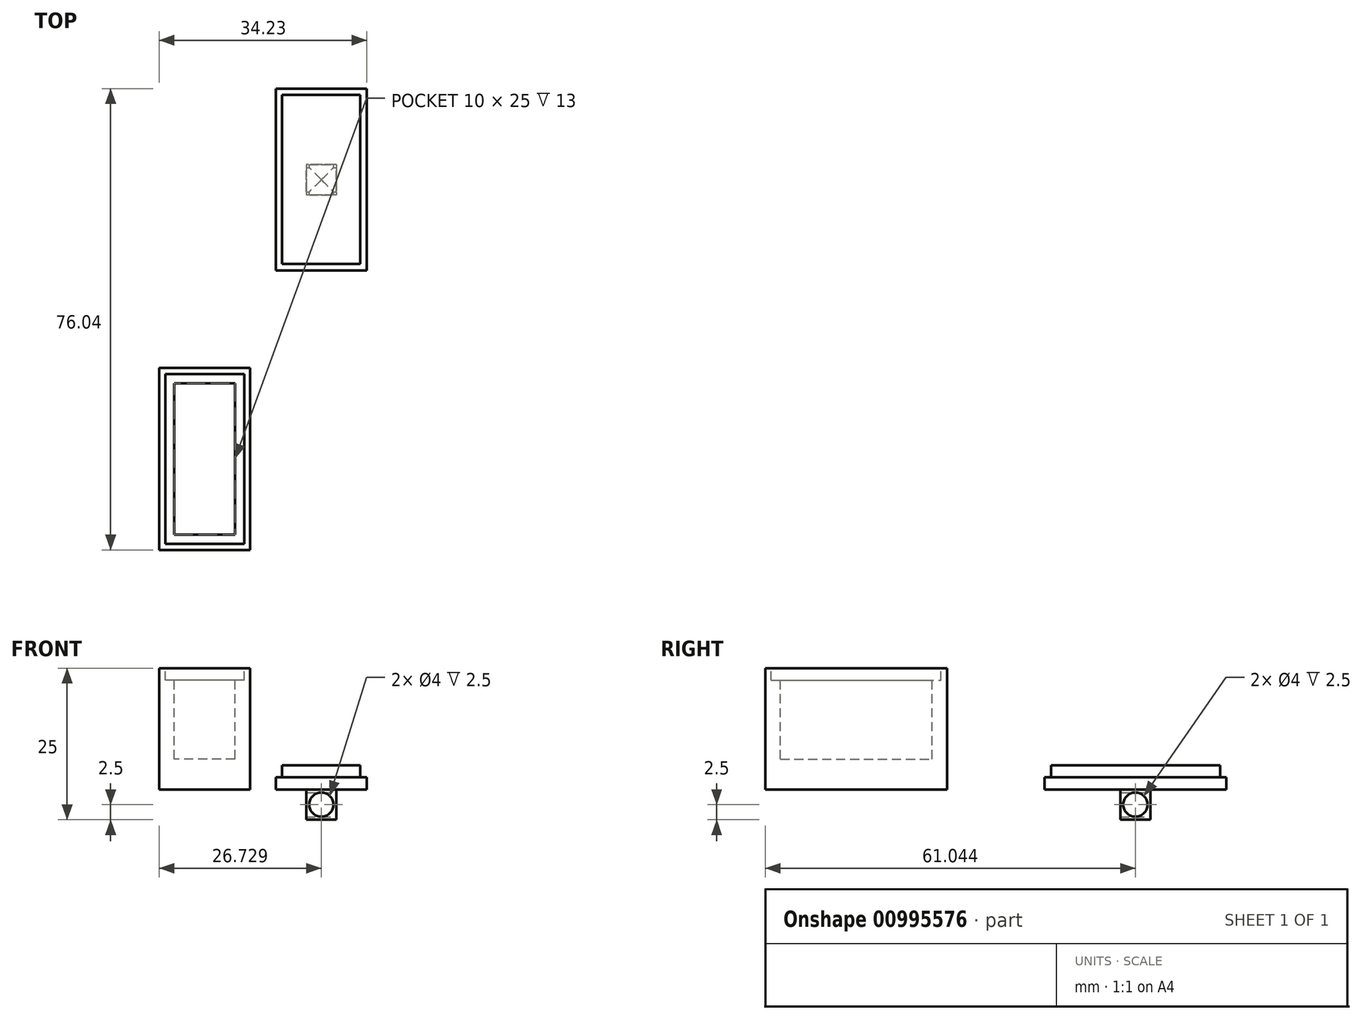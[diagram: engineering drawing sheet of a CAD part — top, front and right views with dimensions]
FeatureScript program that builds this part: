
annotation { "Feature Type Name" : "Feature", "Feature Type Description" : "" }
export const myFeature = defineFeature(function(context is Context, id is Id, definition is map)
    precondition{}
    {
        {
            var Q0;
            Q0=qCreatedBy(makeId("Top.planeOp"),FACE);
            var sketch = newSketch(context, id + "F0", { "sketchPlane" : qUnion([Q0])});
            skLineSegment(sketch, "E0.bottom", {"start": v(7.5, -15) * mm, "end": v(-7.5, -15) * mm});
            skLineSegment(sketch, "E0.top", {"start": v(7.5, 15) * mm, "end": v(-7.5, 15) * mm});
            skLineSegment(sketch, "E0.left", {"start": v(7.5, -15) * mm, "end": v(7.5, 15) * mm});
            skLineSegment(sketch, "E0.right", {"start": v(-7.5, -15) * mm, "end": v(-7.5, 15) * mm});
            skPoint(sketch, "E0.middle", {"position": v(0, 0) * mm});
            skSolve(sketch);
        }
        {
            var Q0;
            Q0=makeQuery(id+"F0.imprint","IMPRINT",FACE,{"disambiguationData":[TD([[makeQuery(id+"F0.imprint","IMPRINT",EDGE,{"derivedFrom":sQuery(id+"F0.wireOp",EDGE,"E0.bottom")}),-1.0]])]});
            extrude(context, id + "F1", {"entities" : qUnion([Q0]), "depth" : 20 * mm, "offsetDistance" : 25 * mm});
        }
        {
            var Q0;
            Q0=makeQuery(id+"F1.opExtrude","CAP_FACE",FACE,{"disambiguationData":[OSD([sQuery(id+"F0.wireOp",EDGE,"E0.bottom"),sQuery(id+"F0.wireOp",EDGE,"E0.top"),sQuery(id+"F0.wireOp",EDGE,"E0.left"),sQuery(id+"F0.wireOp",EDGE,"E0.right")])],"isStart":false});
            var sketch = newSketch(context, id + "F2", { "sketchPlane" : qUnion([Q0])});
            skLineSegment(sketch, "E1.bottom", {"start": v(5, -12.5) * mm, "end": v(-5, -12.5) * mm});
            skLineSegment(sketch, "E1.top", {"start": v(5, 12.5) * mm, "end": v(-5, 12.5) * mm});
            skLineSegment(sketch, "E1.left", {"start": v(5, -12.5) * mm, "end": v(5, 12.5) * mm});
            skLineSegment(sketch, "E1.right", {"start": v(-5, -12.5) * mm, "end": v(-5, 12.5) * mm});
            skPoint(sketch, "E1.middle", {"position": v(0, 0) * mm});
            skSolve(sketch);
        }
        {
            var Q0;
            Q0 = qSketchRegion(id + "F2", true);
            extrude(context, id + "F3", {"entities" : qUnion([Q0]), "operationType" : NewBodyOperationType.REMOVE, "oppositeDirection" : true, "depth" : 15 * mm, "offsetDistance" : 25 * mm});
        }
        {
            var Q0;
            Q0=makeQuery(id+"F1.opExtrude","CAP_FACE",FACE,{"disambiguationData":[OSD([sQuery(id+"F0.wireOp",EDGE,"E0.bottom"),sQuery(id+"F0.wireOp",EDGE,"E0.top"),sQuery(id+"F0.wireOp",EDGE,"E0.left"),sQuery(id+"F0.wireOp",EDGE,"E0.right")])],"isStart":false});
            var sketch = newSketch(context, id + "F4", { "sketchPlane" : qUnion([Q0])});
            skLineSegment(sketch, "E2.bottom", {"start": v(6.5, -14) * mm, "end": v(-6.5, -14) * mm});
            skLineSegment(sketch, "E2.top", {"start": v(6.5, 14) * mm, "end": v(-6.5, 14) * mm});
            skLineSegment(sketch, "E2.left", {"start": v(6.5, -14) * mm, "end": v(6.5, 14) * mm});
            skLineSegment(sketch, "E2.right", {"start": v(-6.5, -14) * mm, "end": v(-6.5, 14) * mm});
            skPoint(sketch, "E2.middle", {"position": v(0, 0) * mm});
            skSolve(sketch);
        }
        {
            var Q0;
            Q0=makeQuery(id+"F4.imprint","IMPRINT",FACE,{"disambiguationData":[TD([[makeQuery(id+"F4.imprint","IMPRINT",EDGE,{"derivedFrom":sQuery(id+"F4.wireOp",EDGE,"E2.bottom")}),-1.0]])]});
            extrude(context, id + "F5", {"entities" : qUnion([Q0]), "operationType" : NewBodyOperationType.REMOVE, "oppositeDirection" : true, "depth" : 2 * mm, "offsetDistance" : 25 * mm});
        }
        {
            var Q0;
            Q0=qCreatedBy(makeId("Top.planeOp"),FACE);
            var sketch = newSketch(context, id + "F6", { "sketchPlane" : qUnion([Q0])});
            skLineSegment(sketch, "E3.bottom", {"start": v(26.73, 61.04) * mm, "end": v(11.73, 61.04) * mm});
            skLineSegment(sketch, "E3.top", {"start": v(26.73, 31.04) * mm, "end": v(11.73, 31.04) * mm});
            skLineSegment(sketch, "E3.left", {"start": v(26.73, 61.04) * mm, "end": v(26.73, 31.04) * mm});
            skLineSegment(sketch, "E3.right", {"start": v(11.73, 61.04) * mm, "end": v(11.73, 31.04) * mm});
            skLineSegment(sketch, "E4", {"start": v(12.73, 60.04) * mm, "end": v(12.73, 32.14) * mm});
            skLineSegment(sketch, "E5", {"start": v(12.73, 32.14) * mm, "end": v(25.63, 32.14) * mm});
            skLineSegment(sketch, "E6", {"start": v(25.63, 32.14) * mm, "end": v(25.63, 60.04) * mm});
            skLineSegment(sketch, "E7", {"start": v(25.63, 60.04) * mm, "end": v(12.73, 60.04) * mm});
            skSolve(sketch);
        }
        {
            var Q0;
            Q0=makeQuery(id+"F6.imprint","IMPRINT",FACE,{"disambiguationData":[TD([[makeQuery(id+"F6.imprint","IMPRINT",EDGE,{"derivedFrom":sQuery(id+"F6.wireOp",EDGE,"E3.bottom")}),1.0]])]});
            var Q1;
            Q1=makeQuery(id+"F6.imprint","IMPRINT",FACE,{"disambiguationData":[TD([[makeQuery(id+"F6.imprint","IMPRINT",EDGE,{"derivedFrom":sQuery(id+"F6.wireOp",EDGE,"E4")}),1.0]])]});
            extrude(context, id + "F7", {"entities" : qUnion([Q0, Q1]), "depth" : 2 * mm, "offsetDistance" : 25 * mm});
        }
        {
            var Q0;
            Q0=makeQuery(id+"F6.imprint","IMPRINT",FACE,{"disambiguationData":[TD([[makeQuery(id+"F6.imprint","IMPRINT",EDGE,{"derivedFrom":sQuery(id+"F6.wireOp",EDGE,"E4")}),1.0]])]});
            extrude(context, id + "F8", {"entities" : qUnion([Q0]), "operationType" : NewBodyOperationType.ADD, "depth" : 4 * mm, "offsetDistance" : 25 * mm});
        }
        {
            var Q0;
            Q0=makeQuery(id+"F7.opExtrude","CAP_FACE",FACE,{"disambiguationData":[OSD([sQuery(id+"F6.wireOp",EDGE,"E3.bottom"),sQuery(id+"F6.wireOp",EDGE,"E3.top"),sQuery(id+"F6.wireOp",EDGE,"E3.left"),sQuery(id+"F6.wireOp",EDGE,"E3.right")])],"isStart":true});
            var sketch = newSketch(context, id + "F9", { "sketchPlane" : qUnion([Q0])});
            skLineSegment(sketch, "E8", {"start": v(11.73, -31.04) * mm, "end": v(26.73, -61.04) * mm});
            skLineSegment(sketch, "E9", {"start": v(11.73, -61.04) * mm, "end": v(26.73, -31.04) * mm});
            skLineSegment(sketch, "E10.bottom", {"start": v(21.73, -48.54) * mm, "end": v(16.73, -48.54) * mm});
            skLineSegment(sketch, "E10.top", {"start": v(21.73, -43.54) * mm, "end": v(16.73, -43.54) * mm});
            skLineSegment(sketch, "E10.left", {"start": v(21.73, -48.54) * mm, "end": v(21.73, -43.54) * mm});
            skLineSegment(sketch, "E10.right", {"start": v(16.73, -48.54) * mm, "end": v(16.73, -43.54) * mm});
            skPoint(sketch, "E10.middle", {"position": v(19.23, -46.04) * mm});
            skSolve(sketch);
        }
        {
            var Q0;
            Q0 = qSketchRegion(id + "F9", true);
            extrude(context, id + "F10", {"entities" : qUnion([Q0]), "operationType" : NewBodyOperationType.ADD, "depth" : 5 * mm, "offsetDistance" : 25 * mm});
        }
        {
            var Q0;
            Q0=makeQuery(id+"F10.opExtrude","SWEPT_FACE",FACE,{"disambiguationData":[OSD([sQuery(id+"F9.wireOp",EDGE,"E10.bottom")])]});
            var sketch = newSketch(context, id + "F11", { "sketchPlane" : qUnion([Q0])});
            skLineSegment(sketch, "E11", {"start": v(-21.73, 0) * mm, "end": v(-16.73, -5) * mm});
            skLineSegment(sketch, "E12", {"start": v(-21.73, -5) * mm, "end": v(-16.73, 0) * mm});
            skCircle(sketch, "E13", {"center": v(-19.23, -2.5) * mm, "radius": 2 * mm});
            skSolve(sketch);
        }
        {
            var Q0;
            Q0=sQuery(id+"F11.wireOp",VERTEX,"E13.center");
            var Q1;
            Q1=makeQuery(id+"F7.opExtrude","SWEPT_BODY",BODY,{"disambiguationData":[OSD([sQuery(id+"F6.wireOp",EDGE,"E3.bottom"),sQuery(id+"F6.wireOp",EDGE,"E3.top"),sQuery(id+"F6.wireOp",EDGE,"E3.left"),sQuery(id+"F6.wireOp",EDGE,"E3.right")])]});
            hole(context, id + "F12", {"style" : HoleStyle.SIMPLE, "endStyle" : HoleEndStyle.THROUGH, "holeDiameter" : 4 * mm, "majorDiameter" : 5 * mm, "isTappedThrough" : true, "tappedDepth" : 12 * mm, "tapClearance" : 3, "locations" : qUnion([Q0]), "scope" : qUnion([Q1])});
        }
        {
            var Q0;
            Q0=makeQuery(id+"F10.opExtrude","SWEPT_FACE",FACE,{"disambiguationData":[OSD([sQuery(id+"F9.wireOp",EDGE,"E10.left")])]});
            var sketch = newSketch(context, id + "F13", { "sketchPlane" : qUnion([Q0])});
            skLineSegment(sketch, "E14", {"start": v(43.54, 0) * mm, "end": v(48.54, -5) * mm});
            skLineSegment(sketch, "E15", {"start": v(43.54, -5) * mm, "end": v(48.54, 0) * mm});
            skCircle(sketch, "E16", {"center": v(46.04, -2.5) * mm, "radius": 2 * mm});
            skSolve(sketch);
        }
        {
            var Q0;
            Q0=sQuery(id+"F13.wireOp",VERTEX,"E16.center");
            var Q1;
            Q1=makeQuery(id+"F7.opExtrude","SWEPT_BODY",BODY,{"disambiguationData":[OSD([sQuery(id+"F6.wireOp",EDGE,"E3.bottom"),sQuery(id+"F6.wireOp",EDGE,"E3.top"),sQuery(id+"F6.wireOp",EDGE,"E3.left"),sQuery(id+"F6.wireOp",EDGE,"E3.right")])]});
            hole(context, id + "F14", {"style" : HoleStyle.SIMPLE, "endStyle" : HoleEndStyle.THROUGH, "holeDiameter" : 4 * mm, "majorDiameter" : 5 * mm, "isTappedThrough" : true, "tappedDepth" : 12 * mm, "tapClearance" : 3, "locations" : qUnion([Q0]), "scope" : qUnion([Q1])});
        }
    });
